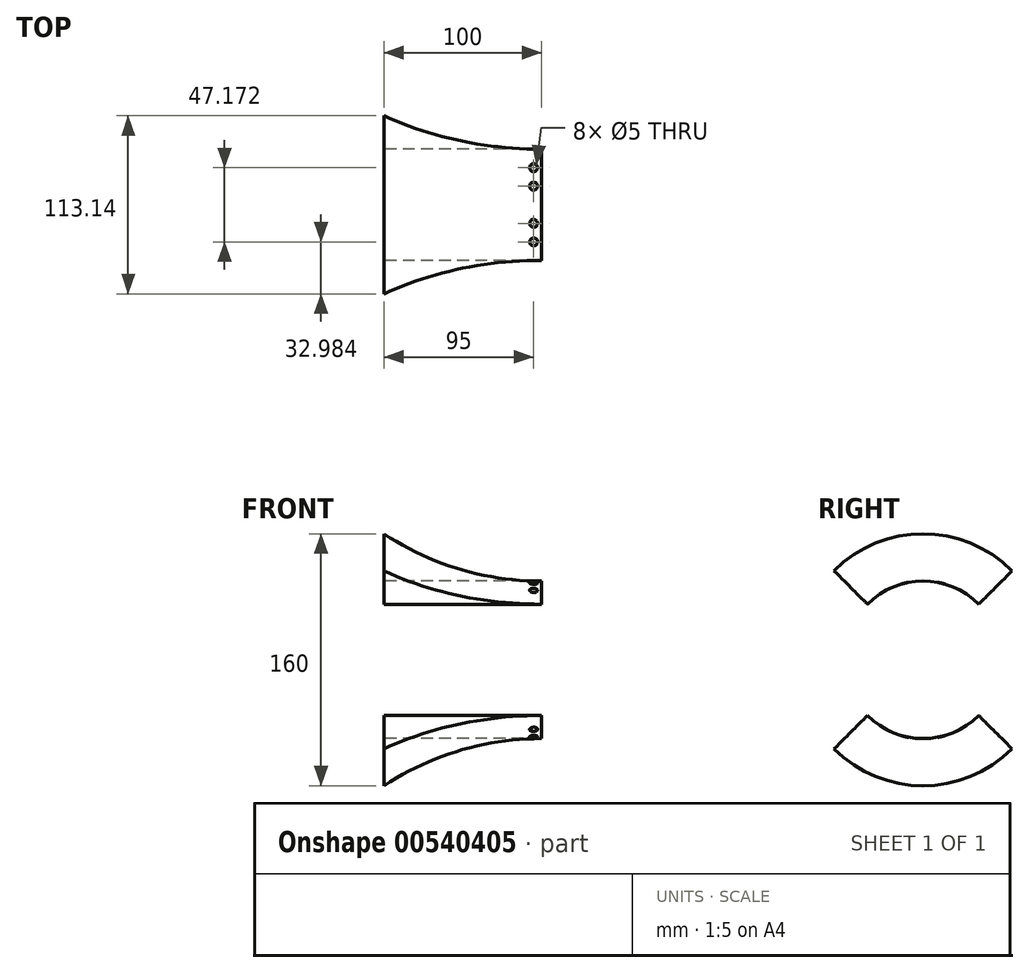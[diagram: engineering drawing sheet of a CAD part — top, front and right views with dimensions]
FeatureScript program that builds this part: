
annotation { "Feature Type Name" : "Feature", "Feature Type Description" : "" }
export const myFeature = defineFeature(function(context is Context, id is Id, definition is map)
    precondition{}
    {
        {
            var Q0;
            Q0=qCreatedBy(makeId("Front.planeOp"),FACE);
            var sketch = newSketch(context, id + "F0", { "sketchPlane" : qUnion([Q0])});
            skLineSegment(sketch, "E0", {"start": v(0, 0) * mm, "end": v(0, 50) * mm});
            skLineSegment(sketch, "E1", {"start": v(0, 50) * mm, "end": v(-100, 50) * mm});
            skLineSegment(sketch, "E2", {"start": v(-100, 50) * mm, "end": v(-100, 80) * mm});
            skArc(sketch, "E3", {"start": v(-100, 80) * mm, "mid": v(-52.2, 57.66) * mm, "end": v(0, 50) * mm});
            skLineSegment(sketch, "E4", {"start": v(-60.09, 0) * mm, "end": v(57.01, 0) * mm});
            skSolve(sketch);
        }
        {
            var Q0;
            Q0 = qSketchRegion(id + "F0", true);
            var Q1;
            Q1=sQuery(id+"F0.wireOp",EDGE,"E4");
            revolve(context, id + "F1", {"entities" : qUnion([Q0]), "axis" : qUnion([Q1]), "revolveType" : RevolveType.TWO_DIRECTIONS, "angle" : 45 * degree, "angleBack" : 315 * degree});
        }
        {
            var Q0;
            Q0=makeQuery(id+"F1.opRevolve","SWEPT_BODY",BODY,{"disambiguationData":[OSD([sQuery(id+"F0.wireOp",EDGE,"E1"),sQuery(id+"F0.wireOp",EDGE,"E2"),sQuery(id+"F0.wireOp",EDGE,"E3")])]});
            var Q1;
            Q1=qCreatedBy(makeId("Top.planeOp"),FACE);
            mirror(context, id + "F2", {"entities" : qUnion([Q0]), "mirrorPlane" : qUnion([Q1])});
        }
        {
            var Q0;
            Q0=qCreatedBy(makeId("Top.planeOp"),FACE);
            var sketch = newSketch(context, id + "F3", { "sketchPlane" : qUnion([Q0])});
            skLineSegment(sketch, "E5", {"start": v(0, 0) * mm, "end": v(0, 11.8) * mm});
            skLineSegment(sketch, "E6", {"start": v(0, 11.8) * mm, "end": v(0, 23.59) * mm});
            skLineSegment(sketch, "E7", {"start": v(0, 11.8) * mm, "end": v(-5, 11.8) * mm});
            skLineSegment(sketch, "E8", {"start": v(0, 23.59) * mm, "end": v(-5, 23.59) * mm});
            skCircle(sketch, "E9", {"center": v(-5, 11.8) * mm, "radius": 2.5 * mm});
            skCircle(sketch, "E10", {"center": v(-5, 23.59) * mm, "radius": 2.5 * mm});
            skLineSegment(sketch, "E11", {"start": v(0, 0) * mm, "end": v(0, -11.8) * mm});
            skLineSegment(sketch, "E12", {"start": v(0, -11.8) * mm, "end": v(0, -23.59) * mm});
            skLineSegment(sketch, "E13", {"start": v(0, -11.8) * mm, "end": v(-5, -11.8) * mm});
            skLineSegment(sketch, "E14", {"start": v(0, -23.59) * mm, "end": v(-5, -23.59) * mm});
            skCircle(sketch, "E15", {"center": v(-5, -11.8) * mm, "radius": 2.5 * mm});
            skCircle(sketch, "E16", {"center": v(-5, -23.59) * mm, "radius": 2.5 * mm});
            skSolve(sketch);
        }
        {
            var Q0;
            Q0 = qSketchRegion(id + "F3", true);
            extrude(context, id + "F4", {"entities" : qUnion([Q0]), "operationType" : NewBodyOperationType.REMOVE, "oppositeDirection" : true, "depth" : 150 * mm, "offsetDistance" : 25 * mm});
        }
        {
            var Q0;
            Q0 = qSketchRegion(id + "F3", true);
            extrude(context, id + "F5", {"entities" : qUnion([Q0]), "operationType" : NewBodyOperationType.REMOVE, "depth" : 150 * mm, "offsetDistance" : 25 * mm});
        }
    });
